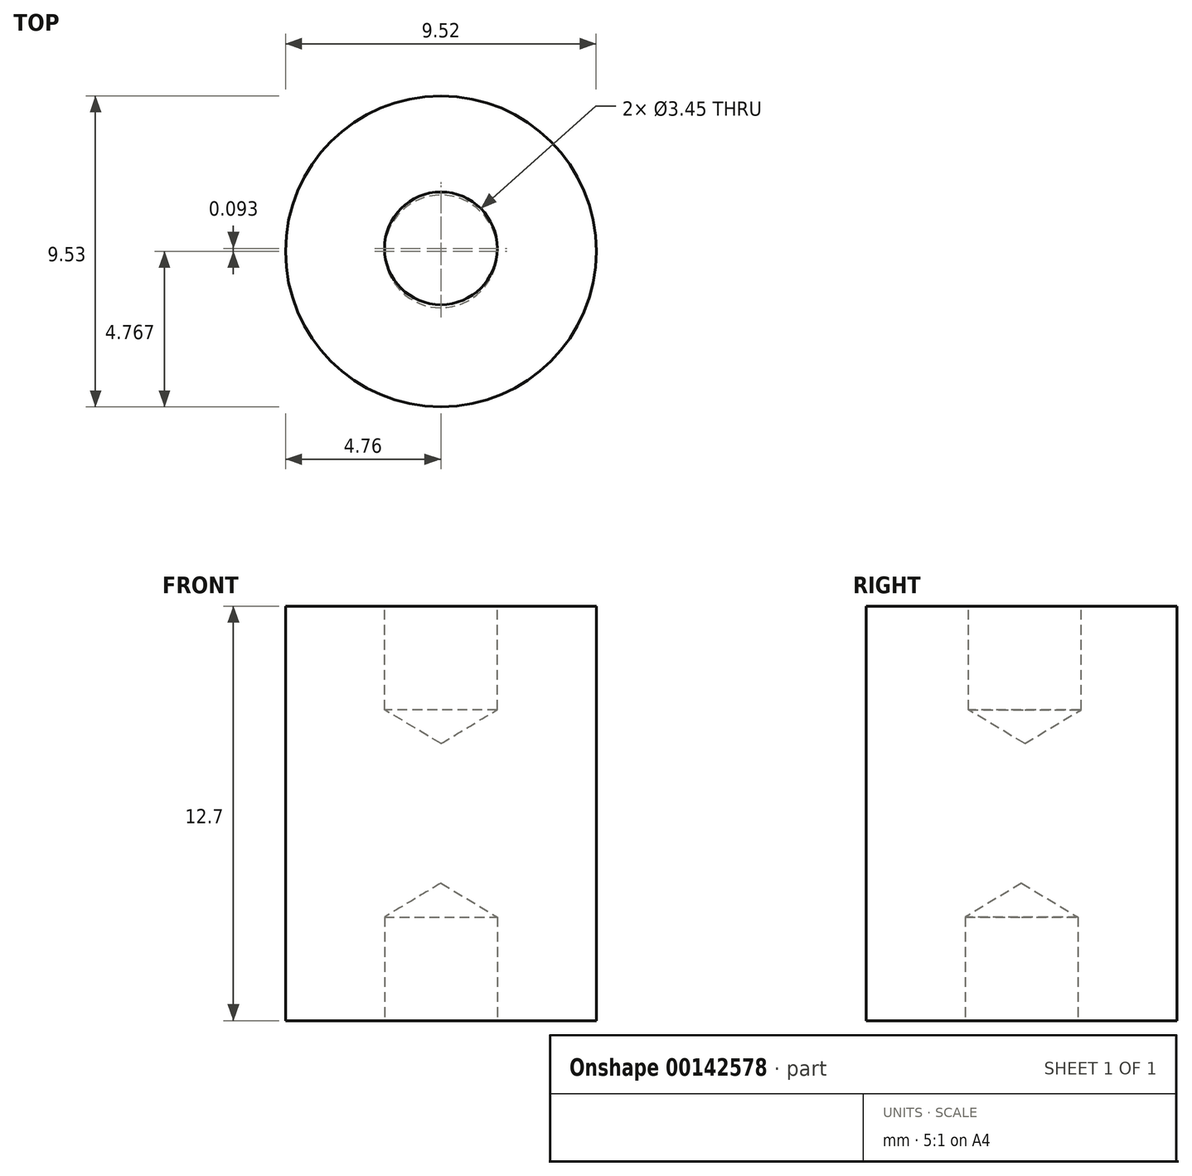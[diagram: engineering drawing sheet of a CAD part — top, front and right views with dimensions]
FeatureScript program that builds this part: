
annotation { "Feature Type Name" : "Feature", "Feature Type Description" : "" }
export const myFeature = defineFeature(function(context is Context, id is Id, definition is map)
    precondition{}
    {
        {
            var Q0;
            Q0=qCreatedBy(makeId("Top.planeOp"),FACE);
            var sketch = newSketch(context, id + "F0", { "sketchPlane" : qUnion([Q0])});
            skCircle(sketch, "E0", {"center": v(0, -0.1) * mm, "radius": 4.76 * mm});
            skSolve(sketch);
        }
        {
            var Q0;
            Q0=makeQuery(id+"F0.imprint","IMPRINT",FACE,{"disambiguationData":[TD([[makeQuery(id+"F0.imprint","IMPRINT",EDGE,{"derivedFrom":sQuery(id+"F0.wireOp",EDGE,"E0")}),1.0]])]});
            extrude(context, id + "F1", {"entities" : qUnion([Q0]), "depth" : 12.7 * mm});
        }
        {
            var Q0;
            Q0=makeQuery(id+"F1.opExtrude","CAP_FACE",FACE,{"disambiguationData":[OSD([sQuery(id+"F0.wireOp",EDGE,"E0")])],"isStart":false});
            var sketch = newSketch(context, id + "F2", { "sketchPlane" : qUnion([Q0])});
            skPoint(sketch, "E1", {"position": v(0, 0) * mm});
            skLineSegment(sketch, "E2", {"start": v(0, 0) * mm, "end": v(0, 4.67) * mm});
            skLineSegment(sketch, "E3", {"start": v(0, 0) * mm, "end": v(4.76, 0) * mm});
            skSolve(sketch);
        }
        {
            var Q0;
            Q0=sQuery(id+"F2.wireOp",VERTEX,"E1");
            var Q1;
            Q1=makeQuery(id+"F1.opExtrude","SWEPT_BODY",BODY,{"disambiguationData":[OSD([sQuery(id+"F0.wireOp",EDGE,"E0")])]});
            hole(context, id + "F3", {"style" : HoleStyle.SIMPLE, "endStyle" : HoleEndStyle.BLIND, "standardTappedOrClearance" : lookupTablePath({ "standard" : "ANSI", "engagement" : "75%", "pitch" : "32 tpi", "size" : "#8", "type" : "Tapped" }), "standardBlindInLast" : lookupTablePath({ "standard" : "ANSI", "engagement" : "75%", "pitch" : "32 tpi", "size" : "#8", "type" : "Tapped" }), "holeDiameter" : 3.45 * mm, "holeDepth" : 3.17 * mm, "locations" : qUnion([Q0]), "scope" : qUnion([Q1]), "majorDiameter" : 4.17 * mm});
        }
        {
            var Q0;
            Q0=sQuery(id+"F0.wireOp",VERTEX,"E0.center");
            var Q1;
            Q1=makeQuery(id+"F1.opExtrude","SWEPT_BODY",BODY,{"disambiguationData":[OSD([sQuery(id+"F0.wireOp",EDGE,"E0")])]});
            hole(context, id + "F4", {"style" : HoleStyle.SIMPLE, "endStyle" : HoleEndStyle.BLIND, "oppositeDirection" : true, "standardTappedOrClearance" : lookupTablePath({ "standard" : "ANSI", "engagement" : "75%", "pitch" : "32 tpi", "size" : "#8", "type" : "Tapped" }), "standardBlindInLast" : lookupTablePath({ "standard" : "ANSI", "engagement" : "75%", "pitch" : "32 tpi", "size" : "#8", "type" : "Tapped" }), "holeDiameter" : 3.45 * mm, "holeDepth" : 3.17 * mm, "locations" : qUnion([Q0]), "scope" : qUnion([Q1]), "majorDiameter" : 4.17 * mm});
        }
    });
